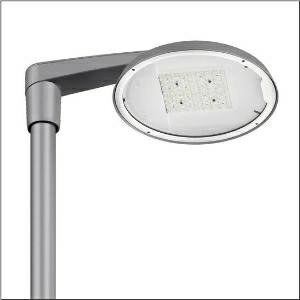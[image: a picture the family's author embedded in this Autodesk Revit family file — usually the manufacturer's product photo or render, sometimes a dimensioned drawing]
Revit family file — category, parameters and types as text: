
# Revit family: dl_r__50_iq_mini___st0_5a_5xa248b41f08le_50d6
name_source: partatom
category: Lighting Fixtures
units: mm (PartAtom-declared; Revit-internal decimal feet)

## family parameters
Cut with Voids When Loaded = No
Host = Face
Light Source = No
Part Type = Normal
Room Calculation Point = No
Round Connector Dimension = Use Diameter
Shared = No

## types (1)
- --- (1 x LED, 10390 lm, 64.1 W, 4000K)
    Apparent Load = 64 VA
    CIE Flux Codes = 41 75 97 100 100
    Color Rendering = 70
    Color Temperature = 4000K
    Default Elevation = 1800 mm
    Description = DL® 50 iQ mini, mast luminaire, primary light control with lens, of PMMA, primary optical cover: cover, of toughened safety glass, transparent, light distribution: ST0.5a, light emission: direct distribution, primary light characteristic: asymmetric, installation type: side-entry, post-top, LED, High Power LED, rated luminous flux: 10.390lm, luminous efficacy: 162lm/W, light colour: 740, colour temperature: 4000K, control gear: iQ Street-Remote, control: optimised constant luminous flux control (CLO 2.0), Desk-Remote (wireless, voltage-free reading and setting of iQ features in the workshop via application-optimized NFC function/RFID function), Light-Fading, Smart-Wire, Night-Set, Lumen-Switch, Temp-Guard, Auto-Match, Street-Remote, mains connection: 230..240V, AC, 50/60Hz, connection cable pre-assembled, cable length: 8,5m, start of lifetime: 64W, end of service life: 67W, reduction: 30W, luminaire housing, of diecast aluminium, powder-coated, Siteco® metallic grey (DB 702S), inclination adjustable: 0°, 5°, 10° (post-top) | 0°, -5°, -10°, -15° (side-entry), please order mast post-top element or mast side-entry element separately, diameter: 500mm, height: 115mm, post-top: for spigot size d x l = 76 x 100mm; with reducer (optional accessory) 60 x 100mm | side-entry: for spigot size d x l = 60 x 100mm; with reducer (optional accessory) 42 x 100mm, mounting height: 4..6m, protection rating (complete): IP66, insulation class (complete): insulation class II (safety insulation), certification: CE, ENEC, ENEC+, VDE, impact resistance: IK08, permissible operating ambient temperature for outdoor applications: -25..+40°C, standard-compliant lighting for roads and squares, packaging unit: 1 piece

Light Distribution: ST0.5a
    Height = 115 mm
    Lamp = 1 x LED
    Lamp Light Flux = 10390 lm
    Lamp Power = 64.1 W
    Lamp count = 1
    Length = 500 mm
    Luminous efficacy = 162 lm/W
    Manufacturer = Siteco
    ModVariant = No
    Model = 5XA248B41F08LE
    Number of Poles = 1
    OnlyDefault = Yes
    Power Factor = 1
    Product Name = DL® 50 iQ mini | ST0.5a
    Product group = mast luminaire | pylon top
    ProductGroupID = 6100
    Protection Class = Protection class II
    Protection Degree = IP 66
    RLX_Detail_Level = 1
    RLX_Emergency_Light_Flux = 0 lm
    RLX_Emergency_Type = 0
    RLX_Emergency_Type_DB = No
    RlxData = <blob elided: 127945 chars, md5=a447824b>
    Socket = socket
    Standby Power = 0 W
    System Light Flux = 10390 lm
    System Power = 64 W
    Type Comments = factory setting: luminous flux: 100 % | dim-lin: 254 | 672 mA
    Type Image = l_1251790.jpg
    URL = http://relux.com
    VarID = @adj_143110
    Voltage = 0 V
    Weight = 0.00 kg
    Width = 0 mm  [stored 0 ft]

note: [stored X ft] marks values corroborated as IEEE doubles in the binary element streams (Revit-internal decimal feet)

## geometry (parser evidence)
native form markers: Blend x4, Sweep x12
no freeform markers — native parametric forms only
